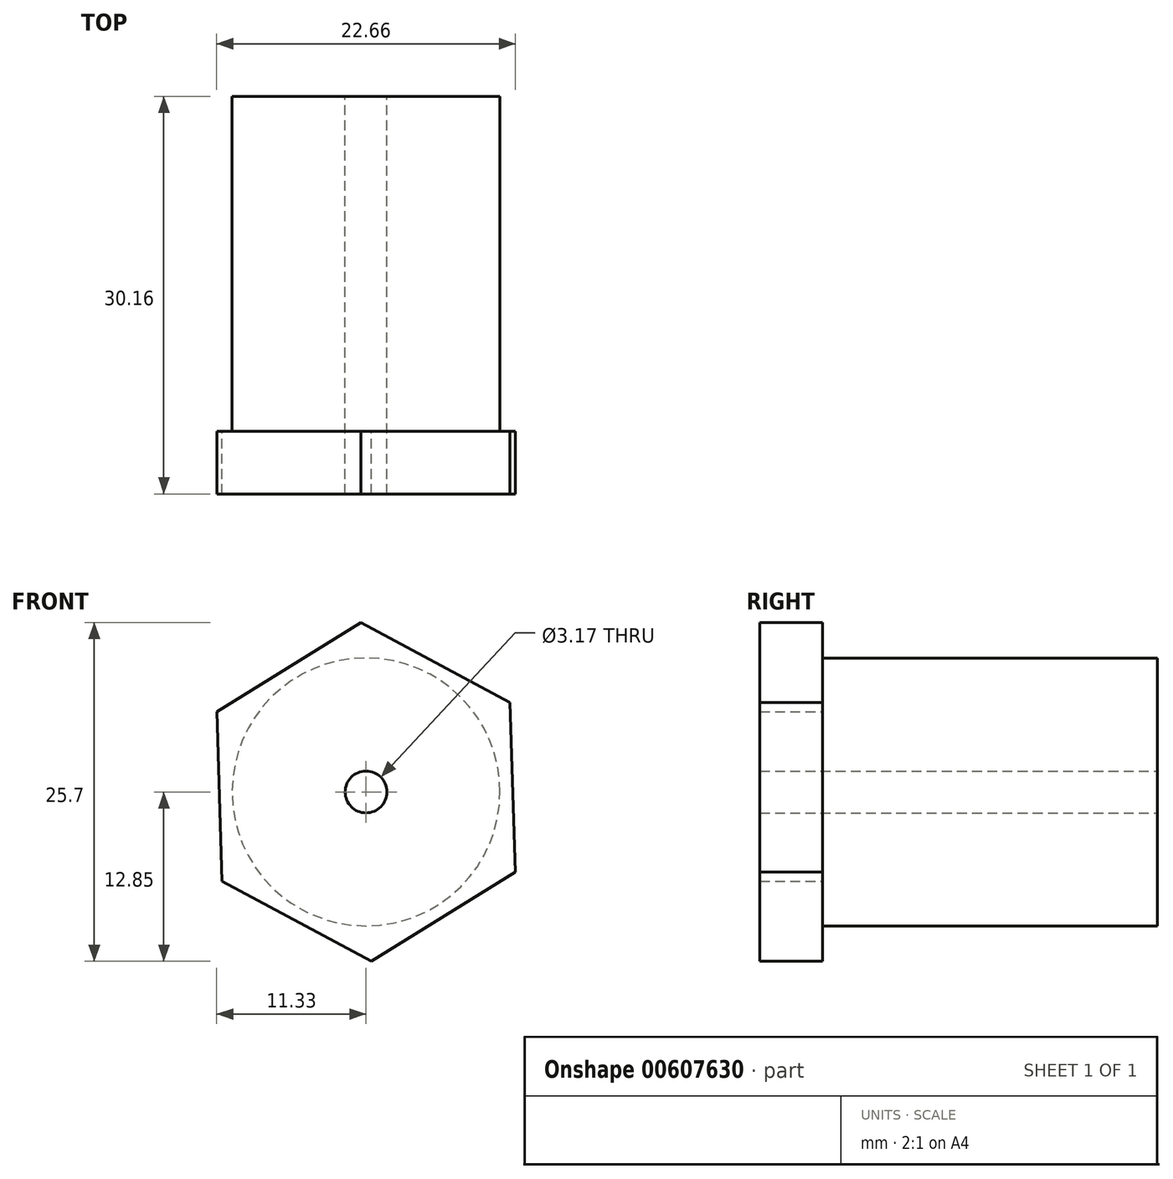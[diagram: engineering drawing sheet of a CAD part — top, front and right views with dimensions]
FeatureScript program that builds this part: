
annotation { "Feature Type Name" : "Feature", "Feature Type Description" : "" }
export const myFeature = defineFeature(function(context is Context, id is Id, definition is map)
    precondition{}
    {
        {
            var Q0;
            Q0=qCreatedBy(makeId("Front.planeOp"),FACE);
            var sketch = newSketch(context, id + "F0", { "sketchPlane" : qUnion([Q0])});
            skCircle(sketch, "E0", {"center": v(0, 0) * mm, "radius": 10.16 * mm});
            skCircle(sketch, "E1", {"center": v(0, 0) * mm, "radius": 1.59 * mm});
            skSolve(sketch);
        }
        {
            var Q0;
            Q0 = qSketchRegion(id + "F0", true);
            extrude(context, id + "F1", {"entities" : qUnion([Q0]), "depth" : 25.4 * mm, "offsetDistance" : 25.4 * mm});
        }
        {
            var Q0;
            Q0=makeQuery(id+"F1.opExtrude","CAP_FACE",FACE,{"disambiguationData":[OSD([sQuery(id+"F0.wireOp",EDGE,"E0"),sQuery(id+"F0.wireOp",EDGE,"E1")])],"isStart":false});
            cPlane(context, id + "F2", {"entities" : qUnion([Q0]), "cplaneType" : CPlaneType.OFFSET, "offset" : 0 * mm, "width" : 152.4 * mm, "height" : 152.4 * mm});
        }
        {
            var Q0;
            Q0=qCreatedBy(id+"F2.planeOp",FACE);
            var sketch = newSketch(context, id + "F3", { "sketchPlane" : qUnion([Q0])});
            skCircle(sketch, "E2.cCircle", {"center": v(0, 0) * mm, "radius": 11.13 * mm, "construction": true});
            skLineSegment(sketch, "E2.0", {"start": v(-0.4, 12.85) * mm, "end": v(10.92, 6.77) * mm});
            skLineSegment(sketch, "E2.1", {"start": v(10.92, 6.77) * mm, "end": v(11.33, -6.07) * mm});
            skLineSegment(sketch, "E2.2", {"start": v(11.33, -6.07) * mm, "end": v(0.4, -12.85) * mm});
            skLineSegment(sketch, "E2.3", {"start": v(0.4, -12.85) * mm, "end": v(-10.92, -6.77) * mm});
            skLineSegment(sketch, "E2.4", {"start": v(-10.92, -6.77) * mm, "end": v(-11.33, 6.07) * mm});
            skLineSegment(sketch, "E2.5", {"start": v(-11.33, 6.07) * mm, "end": v(-0.4, 12.85) * mm});
            skPoint(sketch, "E2.0.midPoint", {"position": v(5.26, 9.8) * mm});
            skCircle(sketch, "E3", {"center": v(0, 0) * mm, "radius": 1.59 * mm});
            skSolve(sketch);
        }
        {
            var Q0;
            Q0 = qSketchRegion(id + "F3", true);
            extrude(context, id + "F4", {"entities" : qUnion([Q0]), "operationType" : NewBodyOperationType.ADD, "depth" : 4.76 * mm, "offsetDistance" : 25.4 * mm});
        }
    });
